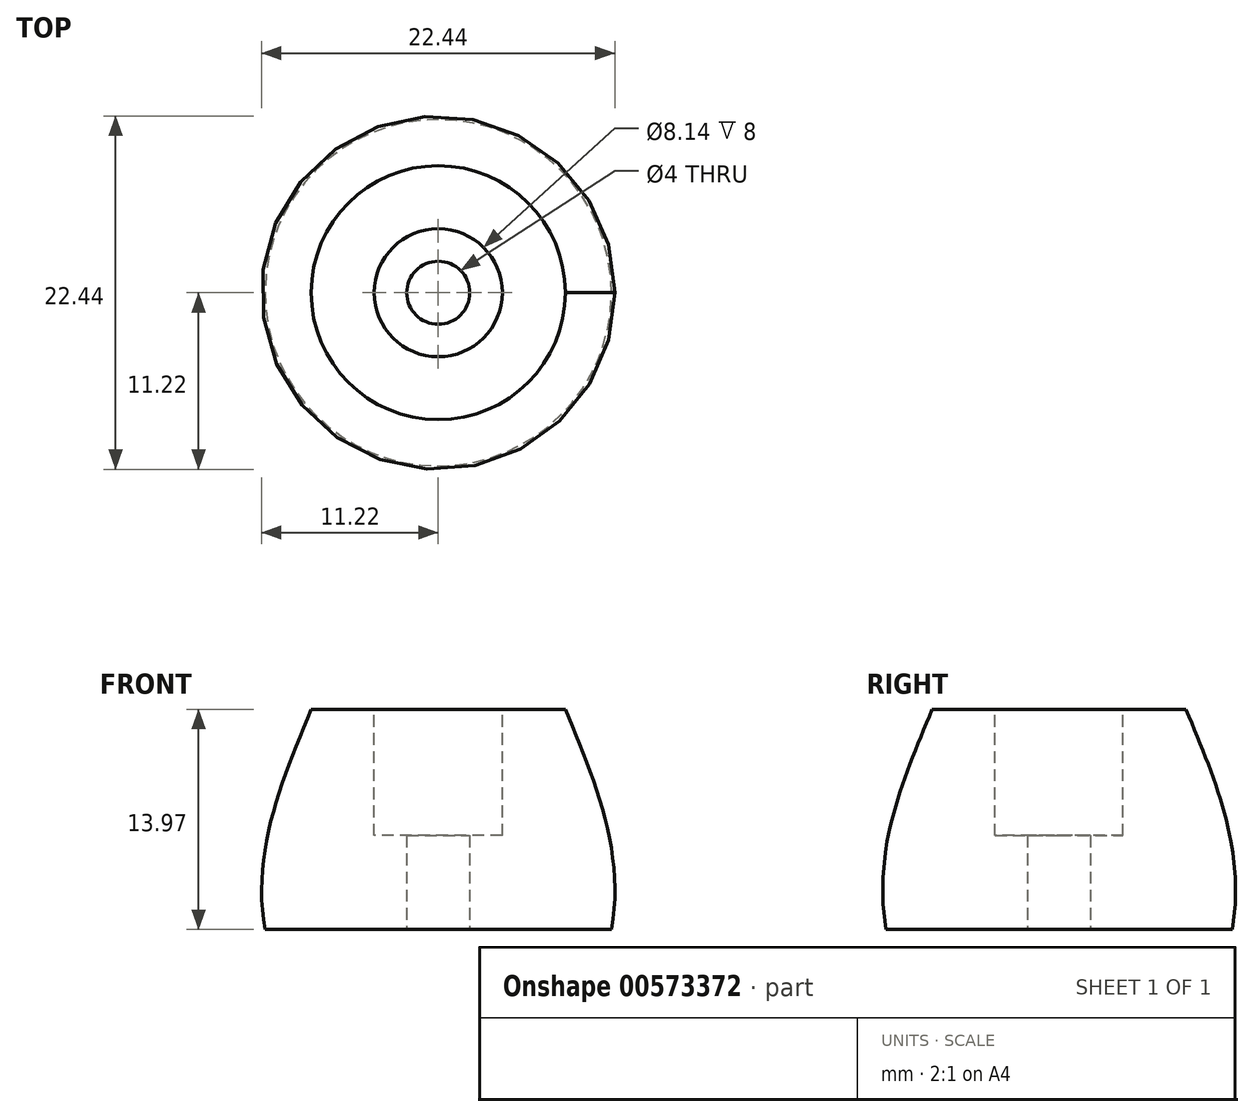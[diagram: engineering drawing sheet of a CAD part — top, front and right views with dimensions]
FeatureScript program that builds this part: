
annotation { "Feature Type Name" : "Feature", "Feature Type Description" : "" }
export const myFeature = defineFeature(function(context is Context, id is Id, definition is map)
    precondition{}
    {
        {
            var Q0;
            Q0=qCreatedBy(makeId("Front.planeOp"),FACE);
            var sketch = newSketch(context, id + "F0", { "sketchPlane" : qUnion([Q0])});
            skLineSegment(sketch, "E0", {"start": v(0, 0) * mm, "end": v(-11, 0) * mm});
            skFitSpline(sketch, "E1", {"points": [v(-11, 0) * mm, v(-8.07, 13.97) * mm], "startDerivative": vector(-2.76, 15.17) * mm, "endDerivative": vector(5.06, 12.28) * mm});
            skLineSegment(sketch, "E2", {"start": v(-8.07, 13.97) * mm, "end": v(-4.07, 13.97) * mm});
            skLineSegment(sketch, "E3", {"start": v(-4.07, 13.97) * mm, "end": v(-4.07, 5.97) * mm});
            skLineSegment(sketch, "E4", {"start": v(-4.07, 5.97) * mm, "end": v(0, 5.97) * mm});
            skLineSegment(sketch, "E5", {"start": v(0, 5.97) * mm, "end": v(0, 0) * mm});
            skSolve(sketch);
        }
        {
            var Q0;
            Q0=makeQuery(id+"F0.imprint","IMPRINT",FACE,{"disambiguationData":[TD([[makeQuery(id+"F0.imprint","IMPRINT",EDGE,{"derivedFrom":sQuery(id+"F0.wireOp",EDGE,"E0")}),-1.0]])]});
            var Q1;
            Q1=sQuery(id+"F0.wireOp",EDGE,"E5");
            revolve(context, id + "F1", {"entities" : qUnion([Q0]), "axis" : qUnion([Q1]), "revolveType" : RevolveType.FULL});
        }
        {
            var Q0;
            Q0=qCreatedBy(makeId("Top.planeOp"),FACE);
            var sketch = newSketch(context, id + "F2", { "sketchPlane" : qUnion([Q0])});
            skCircle(sketch, "E6", {"center": v(0, 0) * mm, "radius": 2 * mm});
            skSolve(sketch);
        }
        {
            var Q0;
            Q0 = qSketchRegion(id + "F2", true);
            extrude(context, id + "F3", {"entities" : qUnion([Q0]), "operationType" : NewBodyOperationType.REMOVE, "depth" : 46.8 * mm, "offsetDistance" : 25 * mm});
        }
    });
